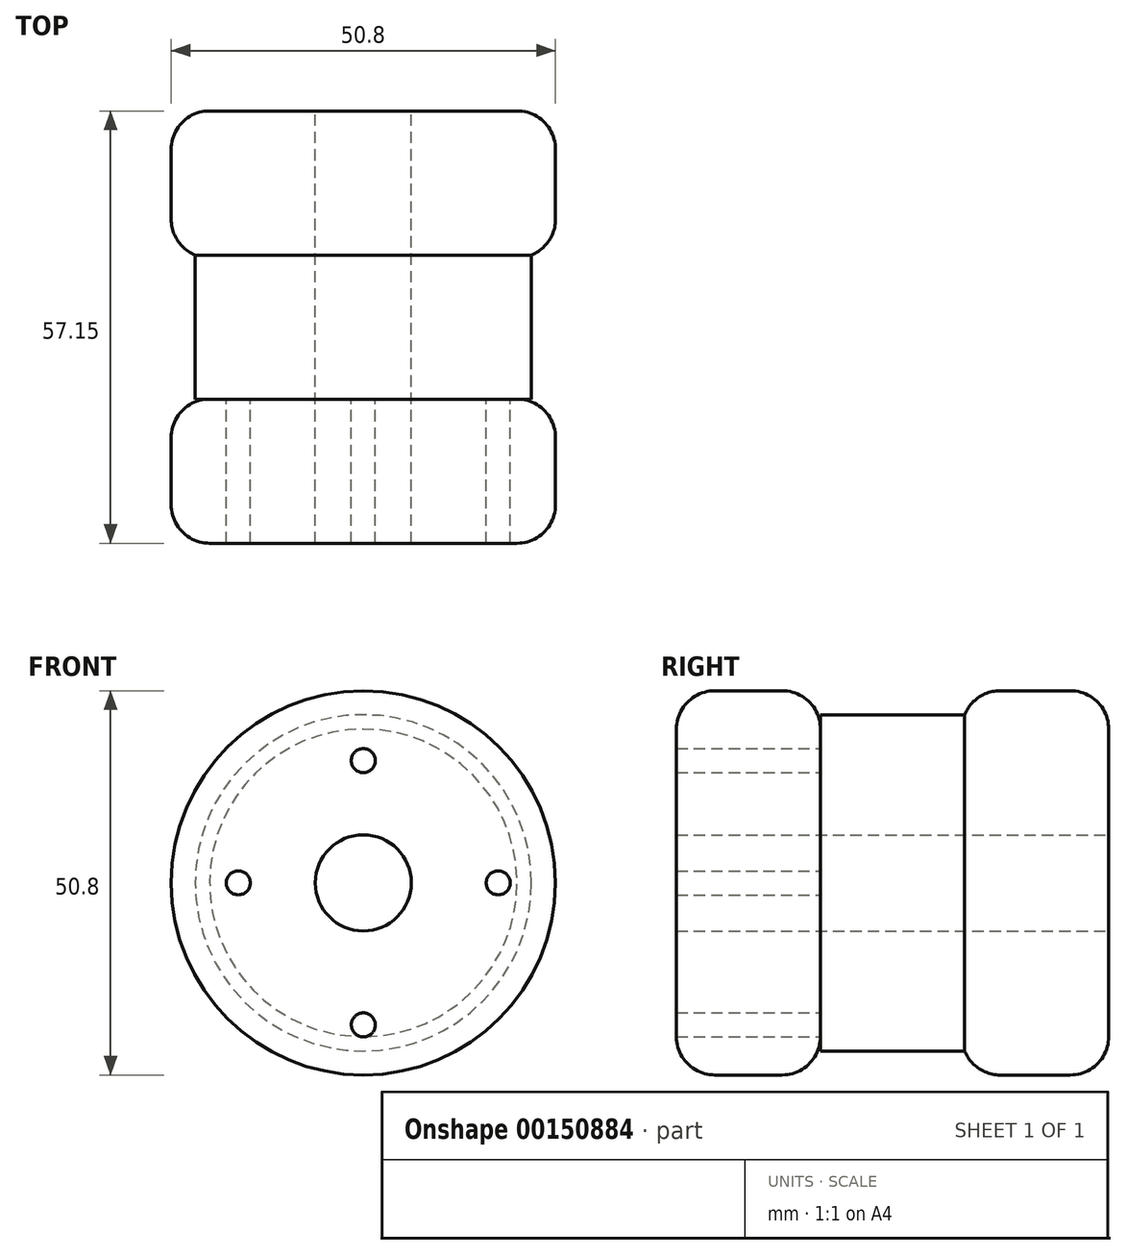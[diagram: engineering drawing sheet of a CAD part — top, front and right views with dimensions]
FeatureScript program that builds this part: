
annotation { "Feature Type Name" : "Feature", "Feature Type Description" : "" }
export const myFeature = defineFeature(function(context is Context, id is Id, definition is map)
    precondition{}
    {
        {
            var Q0;
            Q0=qCreatedBy(makeId("Front.planeOp"),FACE);
            var sketch = newSketch(context, id + "F0", { "sketchPlane" : qUnion([Q0])});
            skCircle(sketch, "E0", {"center": v(0, 0) * mm, "radius": 25.4 * mm});
            skSolve(sketch);
        }
        {
            var Q0;
            Q0=makeQuery(id+"F0.imprint","IMPRINT",FACE,{"disambiguationData":[TD([[makeQuery(id+"F0.imprint","IMPRINT",EDGE,{"derivedFrom":sQuery(id+"F0.wireOp",EDGE,"E0")}),1.0]])]});
            extrude(context, id + "F1", {"entities" : qUnion([Q0]), "depth" : 19.05 * mm});
        }
        {
            var Q0;
            Q0=makeQuery(id+"F1.opExtrude","CAP_FACE",FACE,{"disambiguationData":[OSD([sQuery(id+"F0.wireOp",EDGE,"E0")])],"isStart":true});
            var sketch = newSketch(context, id + "F2", { "sketchPlane" : qUnion([Q0])});
            skCircle(sketch, "E1", {"center": v(0, 16.16) * mm, "radius": 1.59 * mm});
            skCircle(sketch, "E2", {"center": v(16.53, 0) * mm, "radius": 1.59 * mm});
            skCircle(sketch, "E3", {"center": v(0, -18.77) * mm, "radius": 1.59 * mm});
            skCircle(sketch, "E4", {"center": v(-17.84, 0) * mm, "radius": 1.59 * mm});
            skSolve(sketch);
        }
        {
            var Q0;
            Q0 = qSketchRegion(id + "F2", true);
            extrude(context, id + "F3", {"entities" : qUnion([Q0]), "operationType" : NewBodyOperationType.REMOVE, "oppositeDirection" : true, "depth" : 44.45 * mm});
        }
        {
            var Q0;
            Q0=makeQuery(id+"F1.opExtrude","CAP_EDGE",EDGE,{"disambiguationData":[OSD([sQuery(id+"F0.wireOp",EDGE,"E0")])],"isStart":true});
            var Q1;
            Q1=makeQuery(id+"F1.opExtrude","CAP_EDGE",EDGE,{"disambiguationData":[OSD([sQuery(id+"F0.wireOp",EDGE,"E0")])],"isStart":false});
            fillet(context, id + "F4", {"entities" : qUnion([Q0, Q1]), "radius" : 5.08 * mm, "tangentPropagation" : true, "allowEdgeOverflow" : false});
        }
        {
            var Q0;
            Q0=qCreatedBy(makeId("Front.planeOp"),FACE);
            var sketch = newSketch(context, id + "F5", { "sketchPlane" : qUnion([Q0])});
            skCircle(sketch, "E5", {"center": v(0, 0) * mm, "radius": 22.23 * mm});
            skSolve(sketch);
        }
        {
            var Q0;
            Q0 = qSketchRegion(id + "F5", true);
            extrude(context, id + "F6", {"entities" : qUnion([Q0]), "operationType" : NewBodyOperationType.ADD, "oppositeDirection" : true, "depth" : 19.05 * mm});
        }
        {
            var Q0;
            Q0=makeQuery(id+"F6.opExtrude","CAP_FACE",FACE,{"disambiguationData":[OSD([sQuery(id+"F5.wireOp",EDGE,"E5")])],"isStart":false});
            var sketch = newSketch(context, id + "F7", { "sketchPlane" : qUnion([Q0])});
            skCircle(sketch, "E6", {"center": v(0, 0) * mm, "radius": 25.4 * mm});
            skSolve(sketch);
        }
        {
            var Q0;
            Q0 = qSketchRegion(id + "F7", true);
            extrude(context, id + "F8", {"entities" : qUnion([Q0]), "operationType" : NewBodyOperationType.ADD, "depth" : 19.05 * mm});
        }
        {
            var Q0;
            Q0=makeQuery(id+"F8.opExtrude","CAP_EDGE",EDGE,{"disambiguationData":[OSD([sQuery(id+"F7.wireOp",EDGE,"E6")])],"isStart":false});
            var Q1;
            Q1=makeQuery(id+"F8.opExtrude","CAP_EDGE",EDGE,{"disambiguationData":[OSD([sQuery(id+"F7.wireOp",EDGE,"E6")])],"isStart":true});
            fillet(context, id + "F9", {"entities" : qUnion([Q0, Q1]), "radius" : 5.08 * mm, "tangentPropagation" : true, "allowEdgeOverflow" : false});
        }
        {
            var Q0;
            Q0=makeQuery(id+"F8.opExtrude","CAP_FACE",FACE,{"disambiguationData":[OSD([sQuery(id+"F7.wireOp",EDGE,"E6")])],"isStart":false});
            var sketch = newSketch(context, id + "F10", { "sketchPlane" : qUnion([Q0])});
            skCircle(sketch, "E7", {"center": v(0, 0) * mm, "radius": 6.35 * mm});
            skSolve(sketch);
        }
        {
            var Q0;
            Q0 = qSketchRegion(id + "F10", true);
            extrude(context, id + "F11", {"entities" : qUnion([Q0]), "operationType" : NewBodyOperationType.REMOVE, "endBound" : BoundingType.THROUGH_ALL, "oppositeDirection" : true, "depth" : 25.4 * mm});
        }
    });
